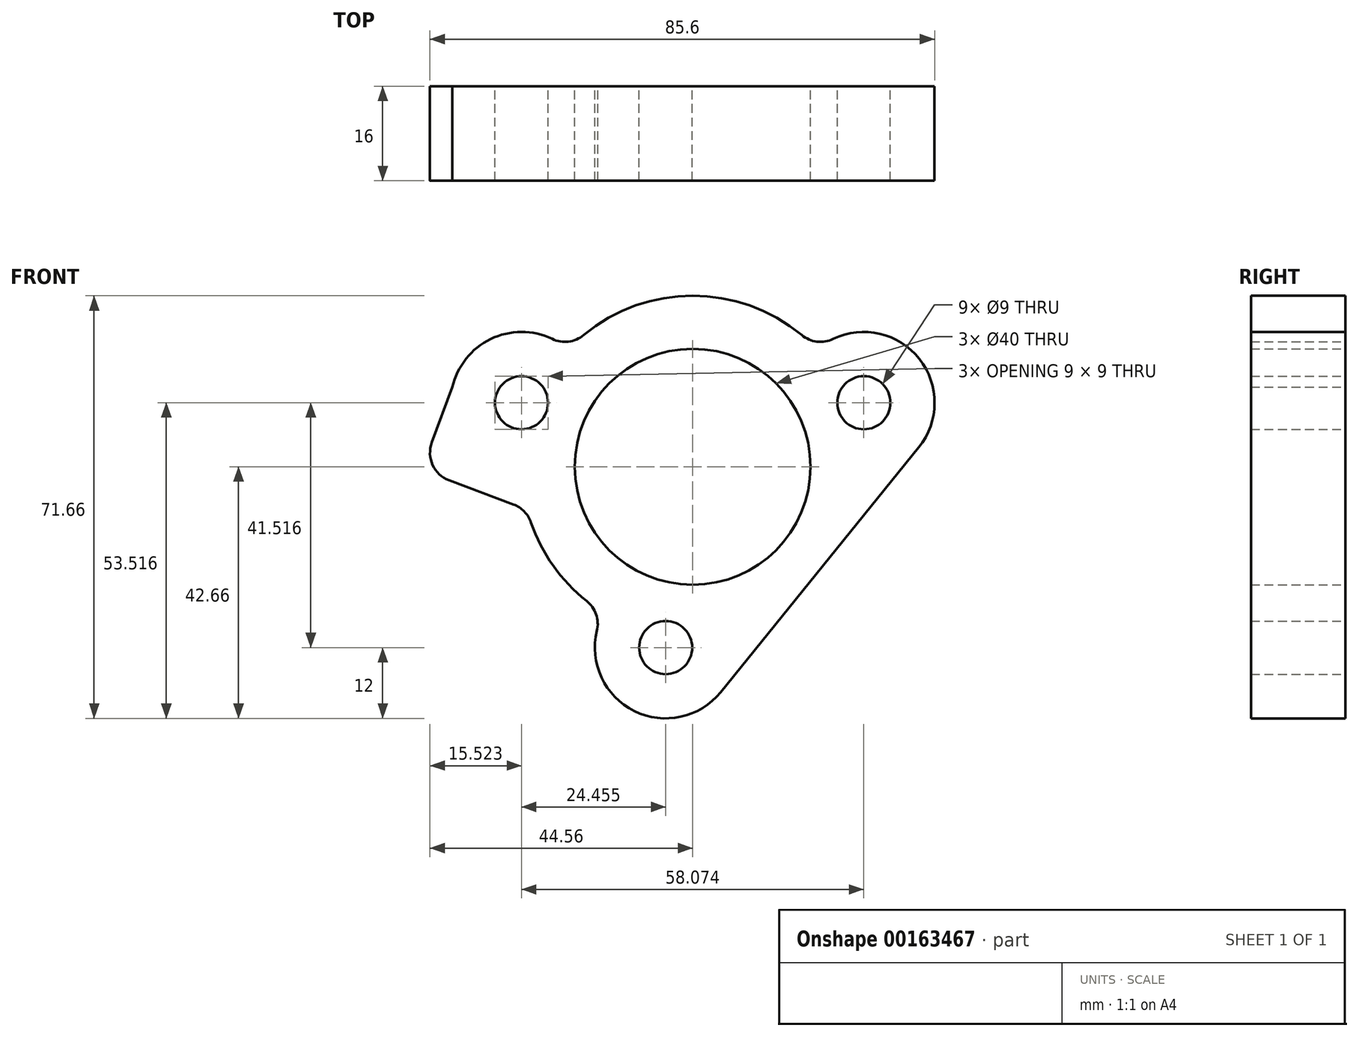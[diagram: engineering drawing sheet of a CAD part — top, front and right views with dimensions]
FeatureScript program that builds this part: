
annotation { "Feature Type Name" : "Feature", "Feature Type Description" : "" }
export const myFeature = defineFeature(function(context is Context, id is Id, definition is map)
    precondition{}
    {
        {
            var Q0;
            Q0=qCreatedBy(makeId("Front.planeOp"),FACE);
            var sketch = newSketch(context, id + "F0", { "sketchPlane" : qUnion([Q0])});
            skCircle(sketch, "E0", {"center": v(0, 0) * mm, "radius": 20 * mm});
            skArc(sketch, "E1", {"start": v(-27.42, -9.45) * mm, "mid": v(-23.66, -16.77) * mm, "end": v(-18, -22.74) * mm});
            skLineSegment(sketch, "E2", {"start": v(0, 0) * mm, "end": v(-4.58, -30.66) * mm, "construction": true});
            skPoint(sketch, "E3", {"position": v(-4.58, -30.66) * mm});
            skLineSegment(sketch, "E4", {"start": v(0, 0) * mm, "end": v(-29.04, 10.86) * mm, "construction": true});
            skPoint(sketch, "E5", {"position": v(-29.04, 10.86) * mm});
            skLineSegment(sketch, "E6", {"start": v(0, 0) * mm, "end": v(29.04, 10.86) * mm, "construction": true});
            skPoint(sketch, "E7", {"position": v(29.04, 10.86) * mm});
            skArc(sketch, "E8", {"start": v(-23.85, 21.68) * mm, "mid": v(-34.27, 21.65) * mm, "end": v(-40.74, 13.49) * mm});
            skArc(sketch, "E9", {"start": v(-16.24, -27.83) * mm, "mid": v(-9.9, -41.42) * mm, "end": v(4.74, -38.21) * mm});
            skArc(sketch, "E10", {"start": v(38.36, 3.3) * mm, "mid": v(38.45, 18.3) * mm, "end": v(23.85, 21.68) * mm});
            skArc(sketch, "E11.trimOffspring", {"start": v(18.5, 22.33) * mm, "mid": v(0, 29) * mm, "end": v(-18.5, 22.33) * mm});
            skPoint(sketch, "E12.visualSharp", {"position": v(-21.12, 19.87) * mm});
            skArc(sketch, "E12.filletArc", {"start": v(-23.85, 21.68) * mm, "mid": v(-21.08, 21.22) * mm, "end": v(-18.5, 22.33) * mm});
            skPoint(sketch, "E13.visualSharp", {"position": v(21.12, 19.87) * mm});
            skArc(sketch, "E13.filletArc", {"start": v(18.5, 22.33) * mm, "mid": v(21.08, 21.22) * mm, "end": v(23.85, 21.68) * mm});
            skPoint(sketch, "E14.visualSharp", {"position": v(-15.05, -24.79) * mm});
            skArc(sketch, "E14.filletArc", {"start": v(-16.24, -27.83) * mm, "mid": v(-16.38, -25.03) * mm, "end": v(-18, -22.74) * mm});
            skLineSegment(sketch, "E15", {"start": v(-40.74, 13.49) * mm, "end": v(-44.25, 4.12) * mm});
            skLineSegment(sketch, "E16", {"start": v(-41.31, -2.31) * mm, "end": v(-30.4, -6.4) * mm});
            skPoint(sketch, "E17.visualSharp", {"position": v(-46, -0.56) * mm});
            skArc(sketch, "E17.filletArc", {"start": v(-44.25, 4.12) * mm, "mid": v(-44.11, 0.3) * mm, "end": v(-41.31, -2.31) * mm});
            skPoint(sketch, "E18.visualSharp", {"position": v(-28.08, -7.26) * mm});
            skArc(sketch, "E18.filletArc", {"start": v(-27.42, -9.45) * mm, "mid": v(-28.56, -7.6) * mm, "end": v(-30.4, -6.4) * mm});
            skLineSegment(sketch, "E19", {"start": v(4.74, -38.21) * mm, "end": v(38.36, 3.3) * mm});
            skSolve(sketch);
        }
        {
            var Q0;
            Q0=makeQuery(id+"F0.imprint","IMPRINT",FACE,{"disambiguationData":[TD([[makeQuery(id+"F0.imprint","IMPRINT",EDGE,{"derivedFrom":sQuery(id+"F0.wireOp",EDGE,"E0")}),-1.0]])]});
            extrude(context, id + "F1", {"entities" : qUnion([Q0]), "depth" : 16 * mm});
        }
        {
            var Q0;
            Q0=sQuery(id+"F0.wireOp",VERTEX,"E7");
            var Q1;
            Q1=sQuery(id+"F0.wireOp",VERTEX,"E5");
            var Q2;
            Q2=sQuery(id+"F0.wireOp",VERTEX,"E3");
            var Q3;
            Q3=makeQuery(id+"F1.opExtrude","SWEPT_BODY",BODY,{"disambiguationData":[OSD([sQuery(id+"F0.wireOp",EDGE,"E0"),sQuery(id+"F0.wireOp",EDGE,"E1"),sQuery(id+"F0.wireOp",EDGE,"E8"),sQuery(id+"F0.wireOp",EDGE,"E9"),sQuery(id+"F0.wireOp",EDGE,"E10"),sQuery(id+"F0.wireOp",EDGE,"E11.trimOffspring"),sQuery(id+"F0.wireOp",EDGE,"E12.filletArc"),sQuery(id+"F0.wireOp",EDGE,"E13.filletArc"),sQuery(id+"F0.wireOp",EDGE,"E14.filletArc"),sQuery(id+"F0.wireOp",EDGE,"E15"),sQuery(id+"F0.wireOp",EDGE,"E16"),sQuery(id+"F0.wireOp",EDGE,"E17.filletArc"),sQuery(id+"F0.wireOp",EDGE,"E18.filletArc"),sQuery(id+"F0.wireOp",EDGE,"E19")])]});
            hole(context, id + "F2", {"style" : HoleStyle.SIMPLE, "endStyle" : HoleEndStyle.THROUGH, "oppositeDirection" : true, "holeDiameter" : 9 * mm, "locations" : qUnion([Q0, Q1, Q2]), "scope" : qUnion([Q3]), "isTappedThrough" : true});
        }
    });
